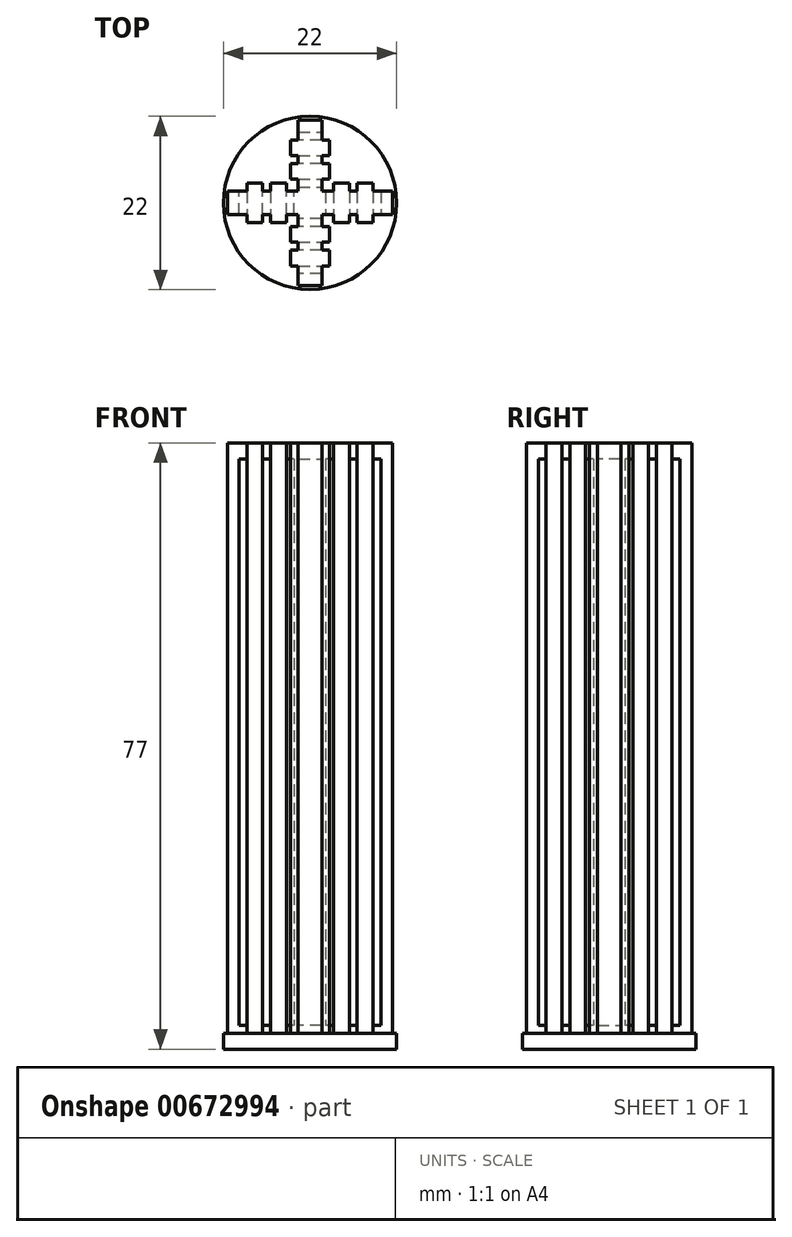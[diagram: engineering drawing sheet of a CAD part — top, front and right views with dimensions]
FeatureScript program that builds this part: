
annotation { "Feature Type Name" : "Feature", "Feature Type Description" : "" }
export const myFeature = defineFeature(function(context is Context, id is Id, definition is map)
    precondition{}
    {
        {
            var Q0;
            Q0=qCreatedBy(makeId("Top.planeOp"),FACE);
            var sketch = newSketch(context, id + "F0", { "sketchPlane" : qUnion([Q0])});
            skCircle(sketch, "E0", {"center": v(0, 0) * mm, "radius": 11 * mm});
            skSolve(sketch);
        }
        {
            var Q0;
            Q0 = qSketchRegion(id + "F0", true);
            extrude(context, id + "F1", {"entities" : qUnion([Q0]), "depth" : 2 * mm, "offsetDistance" : 25 * mm});
        }
        {
            var Q0;
            Q0=makeQuery(id+"F1.opExtrude","CAP_FACE",FACE,{"disambiguationData":[OSD([sQuery(id+"F0.wireOp",EDGE,"E0")])],"isStart":false});
            var sketch = newSketch(context, id + "F2", { "sketchPlane" : qUnion([Q0])});
            skLineSegment(sketch, "E1.bottom", {"start": v(10.5, 1.5) * mm, "end": v(-10.5, 1.5) * mm});
            skLineSegment(sketch, "E1.top", {"start": v(10.5, -1.5) * mm, "end": v(-10.5, -1.5) * mm});
            skLineSegment(sketch, "E1.left", {"start": v(10.5, 1.5) * mm, "end": v(10.5, -1.5) * mm});
            skLineSegment(sketch, "E1.right", {"start": v(-10.5, 1.5) * mm, "end": v(-10.5, -1.5) * mm});
            skPoint(sketch, "E1.middle", {"position": v(0, 0) * mm});
            skLineSegment(sketch, "E2.bottom", {"start": v(-1.5, 10.5) * mm, "end": v(1.5, 10.5) * mm});
            skLineSegment(sketch, "E2.top", {"start": v(-1.5, -10.5) * mm, "end": v(1.5, -10.5) * mm});
            skLineSegment(sketch, "E2.left", {"start": v(-1.5, 10.5) * mm, "end": v(-1.5, -10.5) * mm});
            skLineSegment(sketch, "E2.right", {"start": v(1.5, 10.5) * mm, "end": v(1.5, -10.5) * mm});
            skSolve(sketch);
        }
        {
            var Q0;
            {var subQ0=sQuery(id+"F2.wireOp",EDGE,"E1.right");Q0=makeQuery(id+"F2.imprint","IMPRINT",FACE,{"disambiguationData":[TD([[makeQuery(id+"F2.imprint","IMPRINT",EDGE,{"derivedFrom":subQ0}),1.0]])]});}
            var Q1;
            {var subQ0=sQuery(id+"F2.wireOp",EDGE,"E1.left");Q1=makeQuery(id+"F2.imprint","IMPRINT",FACE,{"disambiguationData":[TD([[makeQuery(id+"F2.imprint","IMPRINT",EDGE,{"derivedFrom":subQ0}),-1.0]])]});}
            var Q2;
            {var subQ5=sQuery(id+"F2.wireOp",EDGE,"E2.bottom");Q2=makeQuery(id+"F2.imprint","IMPRINT",FACE,{"disambiguationData":[TD([[makeQuery(id+"F2.imprint","IMPRINT",EDGE,{"derivedFrom":subQ5}),-1.0]])]});}
            var Q3;
            {var subQ5=sQuery(id+"F2.wireOp",EDGE,"E2.top");Q3=makeQuery(id+"F2.imprint","IMPRINT",FACE,{"disambiguationData":[TD([[makeQuery(id+"F2.imprint","IMPRINT",EDGE,{"derivedFrom":subQ5}),1.0]])]});}
            var Q4;
            {var subQ0=sQuery(id+"F2.wireOp",EDGE,"E2.right");var subQ1=sQuery(id+"F2.wireOp",EDGE,"E1.bottom");var subQ2=makeQuery(id+"F2.imprint","INTERSECT",VERTEX,{"derivedFrom":[subQ1,subQ0]});Q4=makeQuery(id+"F2.imprint","IMPRINT",FACE,{"disambiguationData":[TD([[makeQuery(id+"F2.imprint","IMPRINT",EDGE,{"disambiguationData":[TD([[subQ2,-1.0]])],"derivedFrom":subQ1}),1.0]])]});}
            extrude(context, id + "F3", {"entities" : qUnion([Q0, Q1, Q2, Q3, Q4]), "operationType" : NewBodyOperationType.ADD, "depth" : 1 * mm, "offsetDistance" : 25 * mm});
        }
        {
            var Q0;
            Q0=makeQuery(id+"F1.opExtrude","CAP_FACE",FACE,{"disambiguationData":[OSD([sQuery(id+"F0.wireOp",EDGE,"E0")])],"isStart":false});
            var sketch = newSketch(context, id + "F4", { "sketchPlane" : qUnion([Q0])});
            skLineSegment(sketch, "E3.bottom", {"start": v(10.5, 1.5) * mm, "end": v(9, 1.5) * mm});
            skLineSegment(sketch, "E3.top", {"start": v(10.5, -1.5) * mm, "end": v(9, -1.5) * mm});
            skLineSegment(sketch, "E3.left", {"start": v(10.5, 1.5) * mm, "end": v(10.5, -1.5) * mm});
            skLineSegment(sketch, "E3.right", {"start": v(9, 1.5) * mm, "end": v(9, -1.5) * mm});
            skLineSegment(sketch, "E4.left", {"start": v(8, 1.5) * mm, "end": v(8, -1.5) * mm});
            skLineSegment(sketch, "E4.right", {"start": v(6, 1.5) * mm, "end": v(6, -1.5) * mm});
            skLineSegment(sketch, "E5.left", {"start": v(5, 1.5) * mm, "end": v(5, -1.5) * mm});
            skLineSegment(sketch, "E5.right", {"start": v(3, 1.5) * mm, "end": v(3, -1.5) * mm});
            skLineSegment(sketch, "E6", {"start": v(2, 1.5) * mm, "end": v(2, -1.5) * mm});
            skLineSegment(sketch, "E7", {"start": v(2, 1.5) * mm, "end": v(1.5, 1.5) * mm});
            skLineSegment(sketch, "E8", {"start": v(1.5, 1.5) * mm, "end": v(1.5, 2) * mm});
            skLineSegment(sketch, "E9", {"start": v(8, 1.5) * mm, "end": v(8, 2.5) * mm});
            skLineSegment(sketch, "E10", {"start": v(8, 2.5) * mm, "end": v(6, 2.5) * mm});
            skLineSegment(sketch, "E11", {"start": v(6, 2.5) * mm, "end": v(6, 1.5) * mm});
            skLineSegment(sketch, "E12", {"start": v(5, 1.5) * mm, "end": v(5, 2.5) * mm});
            skLineSegment(sketch, "E13", {"start": v(5, 2.5) * mm, "end": v(3, 2.5) * mm});
            skLineSegment(sketch, "E14", {"start": v(3, 2.5) * mm, "end": v(3, 1.5) * mm});
            skLineSegment(sketch, "E15.MirrorCS", {"start": v(6, -2.5) * mm, "end": v(6, -1.5) * mm});
            skLineSegment(sketch, "E16.MirrorCS", {"start": v(8, -1.5) * mm, "end": v(8, -2.5) * mm});
            skLineSegment(sketch, "E17.MirrorCS", {"start": v(3, -2.5) * mm, "end": v(3, -1.5) * mm});
            skLineSegment(sketch, "E18.MirrorCS", {"start": v(5, -1.5) * mm, "end": v(5, -2.5) * mm});
            skLineSegment(sketch, "E19.MirrorCS", {"start": v(8, -2.5) * mm, "end": v(6, -2.5) * mm});
            skLineSegment(sketch, "E20.MirrorCS", {"start": v(5, -2.5) * mm, "end": v(3, -2.5) * mm});
            skLineSegment(sketch, "E21.1.0", {"start": v(2.5, 8) * mm, "end": v(2.5, 6) * mm});
            skLineSegment(sketch, "E21.1.1", {"start": v(2.5, 5) * mm, "end": v(2.5, 3) * mm});
            skLineSegment(sketch, "E21.1.2", {"start": v(-2.5, 5) * mm, "end": v(-2.5, 3) * mm});
            skLineSegment(sketch, "E21.1.3", {"start": v(2.5, 6) * mm, "end": v(1.5, 6) * mm});
            skLineSegment(sketch, "E21.1.4", {"start": v(2.5, 3) * mm, "end": v(1.5, 3) * mm});
            skLineSegment(sketch, "E21.1.5", {"start": v(1.5, 5) * mm, "end": v(2.5, 5) * mm});
            skLineSegment(sketch, "E21.1.6", {"start": v(-1.5, 10.5) * mm, "end": v(-1.5, 9) * mm});
            skLineSegment(sketch, "E21.1.7", {"start": v(-1.5, 5) * mm, "end": v(-2.5, 5) * mm});
            skLineSegment(sketch, "E21.1.8", {"start": v(1.5, 10.5) * mm, "end": v(1.5, 9) * mm});
            skLineSegment(sketch, "E21.1.9", {"start": v(-1.5, 10.5) * mm, "end": v(1.5, 10.5) * mm});
            skLineSegment(sketch, "E21.1.10", {"start": v(-1.5, 9) * mm, "end": v(1.5, 9) * mm});
            skLineSegment(sketch, "E21.1.11", {"start": v(-2.5, 6) * mm, "end": v(-1.5, 6) * mm});
            skLineSegment(sketch, "E21.1.12", {"start": v(-1.5, 5) * mm, "end": v(1.5, 5) * mm});
            skLineSegment(sketch, "E21.1.13", {"start": v(-1.5, 8) * mm, "end": v(1.5, 8) * mm});
            skLineSegment(sketch, "E21.1.14", {"start": v(-2.5, 3) * mm, "end": v(-1.5, 3) * mm});
            skLineSegment(sketch, "E21.1.15", {"start": v(-2.5, 8) * mm, "end": v(-2.5, 6) * mm});
            skLineSegment(sketch, "E21.1.16", {"start": v(-1.5, 8) * mm, "end": v(-2.5, 8) * mm});
            skLineSegment(sketch, "E21.1.17", {"start": v(-1.5, 1.5) * mm, "end": v(-2, 1.5) * mm});
            skLineSegment(sketch, "E21.1.18", {"start": v(-1.5, 6) * mm, "end": v(1.5, 6) * mm});
            skLineSegment(sketch, "E21.1.19", {"start": v(1.5, 8) * mm, "end": v(2.5, 8) * mm});
            skLineSegment(sketch, "E21.1.20", {"start": v(-1.5, 2) * mm, "end": v(1.5, 2) * mm});
            skLineSegment(sketch, "E21.1.21", {"start": v(-1.5, 3) * mm, "end": v(1.5, 3) * mm});
            skLineSegment(sketch, "E21.1.22", {"start": v(-1.5, 2) * mm, "end": v(-1.5, 1.5) * mm});
            skLineSegment(sketch, "E21.2.0", {"start": v(-8, 2.5) * mm, "end": v(-6, 2.5) * mm});
            skLineSegment(sketch, "E21.2.1", {"start": v(-5, 2.5) * mm, "end": v(-3, 2.5) * mm});
            skLineSegment(sketch, "E21.2.2", {"start": v(-5, -2.5) * mm, "end": v(-3, -2.5) * mm});
            skLineSegment(sketch, "E21.2.3", {"start": v(-6, 2.5) * mm, "end": v(-6, 1.5) * mm});
            skLineSegment(sketch, "E21.2.4", {"start": v(-3, 2.5) * mm, "end": v(-3, 1.5) * mm});
            skLineSegment(sketch, "E21.2.5", {"start": v(-5, 1.5) * mm, "end": v(-5, 2.5) * mm});
            skLineSegment(sketch, "E21.2.6", {"start": v(-10.5, -1.5) * mm, "end": v(-9, -1.5) * mm});
            skLineSegment(sketch, "E21.2.7", {"start": v(-5, -1.5) * mm, "end": v(-5, -2.5) * mm});
            skLineSegment(sketch, "E21.2.8", {"start": v(-10.5, 1.5) * mm, "end": v(-9, 1.5) * mm});
            skLineSegment(sketch, "E21.2.9", {"start": v(-10.5, -1.5) * mm, "end": v(-10.5, 1.5) * mm});
            skLineSegment(sketch, "E21.2.10", {"start": v(-9, -1.5) * mm, "end": v(-9, 1.5) * mm});
            skLineSegment(sketch, "E21.2.11", {"start": v(-6, -2.5) * mm, "end": v(-6, -1.5) * mm});
            skLineSegment(sketch, "E21.2.12", {"start": v(-5, -1.5) * mm, "end": v(-5, 1.5) * mm});
            skLineSegment(sketch, "E21.2.13", {"start": v(-8, -1.5) * mm, "end": v(-8, 1.5) * mm});
            skLineSegment(sketch, "E21.2.14", {"start": v(-3, -2.5) * mm, "end": v(-3, -1.5) * mm});
            skLineSegment(sketch, "E21.2.15", {"start": v(-8, -2.5) * mm, "end": v(-6, -2.5) * mm});
            skLineSegment(sketch, "E21.2.16", {"start": v(-8, -1.5) * mm, "end": v(-8, -2.5) * mm});
            skLineSegment(sketch, "E21.2.17", {"start": v(-1.5, -1.5) * mm, "end": v(-1.5, -2) * mm});
            skLineSegment(sketch, "E21.2.18", {"start": v(-6, -1.5) * mm, "end": v(-6, 1.5) * mm});
            skLineSegment(sketch, "E21.2.19", {"start": v(-8, 1.5) * mm, "end": v(-8, 2.5) * mm});
            skLineSegment(sketch, "E21.2.20", {"start": v(-2, -1.5) * mm, "end": v(-2, 1.5) * mm});
            skLineSegment(sketch, "E21.2.21", {"start": v(-3, -1.5) * mm, "end": v(-3, 1.5) * mm});
            skLineSegment(sketch, "E21.2.22", {"start": v(-2, -1.5) * mm, "end": v(-1.5, -1.5) * mm});
            skLineSegment(sketch, "E21.3.0", {"start": v(-2.5, -8) * mm, "end": v(-2.5, -6) * mm});
            skLineSegment(sketch, "E21.3.1", {"start": v(-2.5, -5) * mm, "end": v(-2.5, -3) * mm});
            skLineSegment(sketch, "E21.3.2", {"start": v(2.5, -5) * mm, "end": v(2.5, -3) * mm});
            skLineSegment(sketch, "E21.3.3", {"start": v(-2.5, -6) * mm, "end": v(-1.5, -6) * mm});
            skLineSegment(sketch, "E21.3.4", {"start": v(-2.5, -3) * mm, "end": v(-1.5, -3) * mm});
            skLineSegment(sketch, "E21.3.5", {"start": v(-1.5, -5) * mm, "end": v(-2.5, -5) * mm});
            skLineSegment(sketch, "E21.3.6", {"start": v(1.5, -10.5) * mm, "end": v(1.5, -9) * mm});
            skLineSegment(sketch, "E21.3.7", {"start": v(1.5, -5) * mm, "end": v(2.5, -5) * mm});
            skLineSegment(sketch, "E21.3.8", {"start": v(-1.5, -10.5) * mm, "end": v(-1.5, -9) * mm});
            skLineSegment(sketch, "E21.3.9", {"start": v(1.5, -10.5) * mm, "end": v(-1.5, -10.5) * mm});
            skLineSegment(sketch, "E21.3.10", {"start": v(1.5, -9) * mm, "end": v(-1.5, -9) * mm});
            skLineSegment(sketch, "E21.3.11", {"start": v(2.5, -6) * mm, "end": v(1.5, -6) * mm});
            skLineSegment(sketch, "E21.3.12", {"start": v(1.5, -5) * mm, "end": v(-1.5, -5) * mm});
            skLineSegment(sketch, "E21.3.13", {"start": v(1.5, -8) * mm, "end": v(-1.5, -8) * mm});
            skLineSegment(sketch, "E21.3.14", {"start": v(2.5, -3) * mm, "end": v(1.5, -3) * mm});
            skLineSegment(sketch, "E21.3.15", {"start": v(2.5, -8) * mm, "end": v(2.5, -6) * mm});
            skLineSegment(sketch, "E21.3.16", {"start": v(1.5, -8) * mm, "end": v(2.5, -8) * mm});
            skLineSegment(sketch, "E21.3.17", {"start": v(1.5, -1.5) * mm, "end": v(2, -1.5) * mm});
            skLineSegment(sketch, "E21.3.18", {"start": v(1.5, -6) * mm, "end": v(-1.5, -6) * mm});
            skLineSegment(sketch, "E21.3.19", {"start": v(-1.5, -8) * mm, "end": v(-2.5, -8) * mm});
            skLineSegment(sketch, "E21.3.20", {"start": v(1.5, -2) * mm, "end": v(-1.5, -2) * mm});
            skLineSegment(sketch, "E21.3.21", {"start": v(1.5, -3) * mm, "end": v(-1.5, -3) * mm});
            skLineSegment(sketch, "E21.3.22", {"start": v(1.5, -2) * mm, "end": v(1.5, -1.5) * mm});
            skPoint(sketch, "E21.center", {"position": v(0, 0) * mm});
            skSolve(sketch);
        }
        {
            var Q0;
            Q0 = qSketchRegion(id + "F4", true);
            extrude(context, id + "F5", {"entities" : qUnion([Q0]), "operationType" : NewBodyOperationType.ADD, "depth" : 75 * mm, "offsetDistance" : 25 * mm});
        }
        {
            var Q0;
            Q0=makeQuery(id+"F5.opExtrude","CAP_FACE",FACE,{"disambiguationData":[OSD([sQuery(id+"F4.wireOp",EDGE,"E6"),sQuery(id+"F4.wireOp",EDGE,"E7"),sQuery(id+"F4.wireOp",EDGE,"E8"),sQuery(id+"F4.wireOp",EDGE,"E21.1.17"),sQuery(id+"F4.wireOp",EDGE,"E21.1.20"),sQuery(id+"F4.wireOp",EDGE,"E21.1.22"),sQuery(id+"F4.wireOp",EDGE,"E21.2.17"),sQuery(id+"F4.wireOp",EDGE,"E21.2.20"),sQuery(id+"F4.wireOp",EDGE,"E21.2.22"),sQuery(id+"F4.wireOp",EDGE,"E21.3.17"),sQuery(id+"F4.wireOp",EDGE,"E21.3.20"),sQuery(id+"F4.wireOp",EDGE,"E21.3.22")])],"isStart":false});
            var sketch = newSketch(context, id + "F6", { "sketchPlane" : qUnion([Q0])});
            skLineSegment(sketch, "E22.0", {"start": v(-1.5, 10.5) * mm, "end": v(-1.5, -10.5) * mm});
            skLineSegment(sketch, "E23.0", {"start": v(-1.5, 10.5) * mm, "end": v(1.5, 10.5) * mm});
            skLineSegment(sketch, "E24.0", {"start": v(1.5, 10.5) * mm, "end": v(1.5, -10.5) * mm});
            skLineSegment(sketch, "E25.0", {"start": v(10.5, 1.5) * mm, "end": v(-10.5, 1.5) * mm});
            skLineSegment(sketch, "E26.0", {"start": v(10.5, -1.5) * mm, "end": v(-10.5, -1.5) * mm});
            skLineSegment(sketch, "E27.0", {"start": v(-1.5, -10.5) * mm, "end": v(1.5, -10.5) * mm});
            skLineSegment(sketch, "E28.0", {"start": v(10.5, 1.5) * mm, "end": v(10.5, -1.5) * mm});
            skLineSegment(sketch, "E29.0", {"start": v(-10.5, 1.5) * mm, "end": v(-10.5, -1.5) * mm});
            skSolve(sketch);
        }
        {
            var Q0;
            Q0 = qSketchRegion(id + "F6", true);
            extrude(context, id + "F7", {"entities" : qUnion([Q0]), "operationType" : NewBodyOperationType.ADD, "oppositeDirection" : true, "depth" : 2 * mm, "offsetDistance" : 25 * mm});
        }
    });
